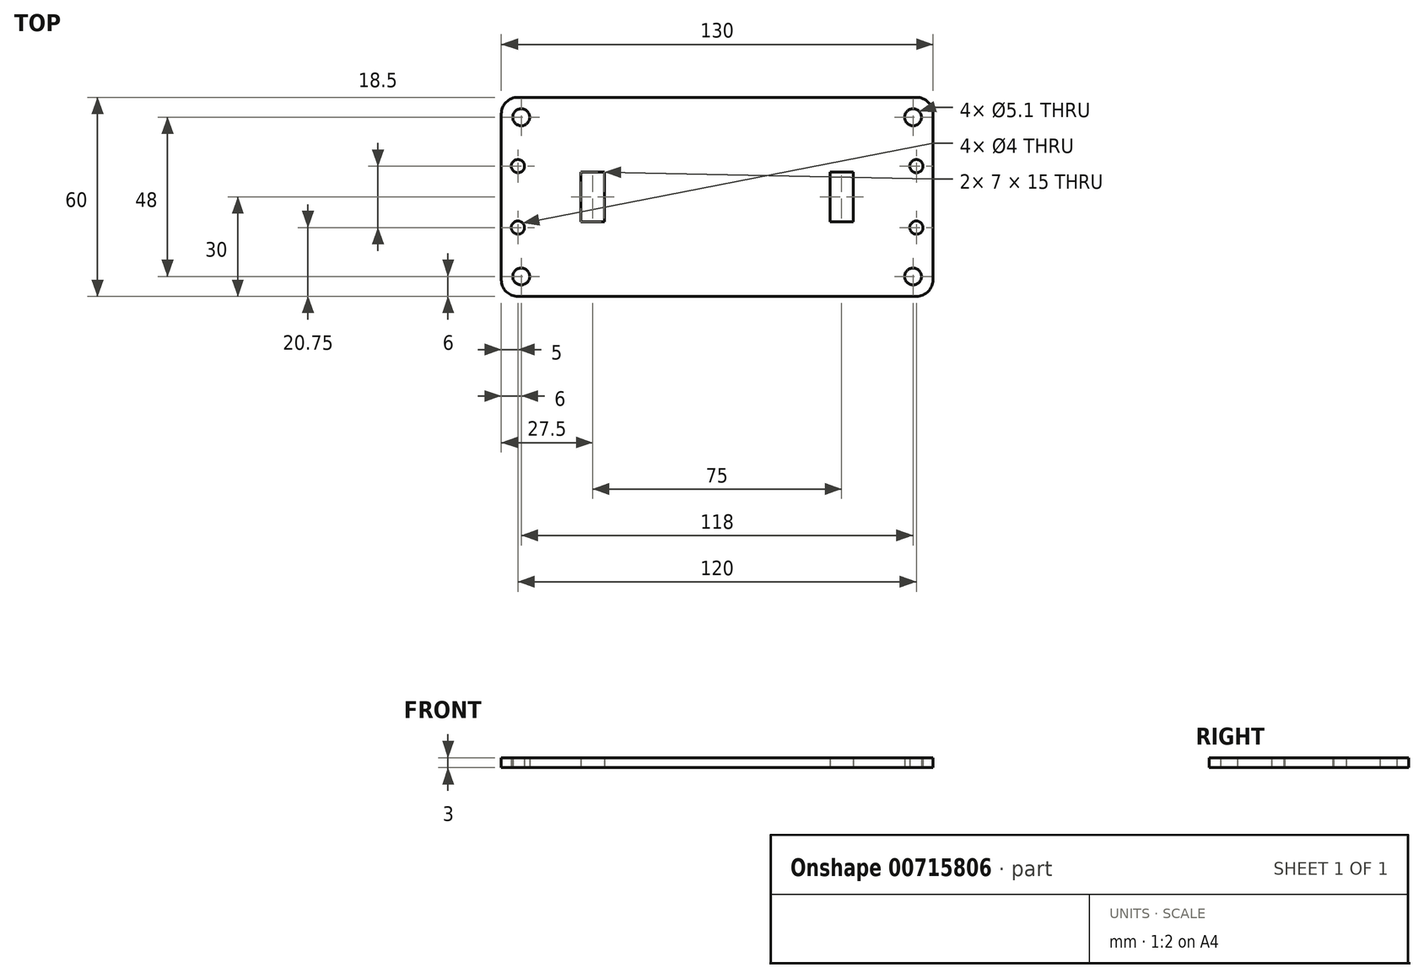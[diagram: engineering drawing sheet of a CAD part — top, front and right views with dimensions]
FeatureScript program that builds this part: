
annotation { "Feature Type Name" : "Feature", "Feature Type Description" : "" }
export const myFeature = defineFeature(function(context is Context, id is Id, definition is map)
    precondition{}
    {
        {
            var Q0;
            Q0=qCreatedBy(makeId("Top.planeOp"),FACE);
            var sketch = newSketch(context, id + "F0", { "sketchPlane" : qUnion([Q0])});
            skLineSegment(sketch, "E0.bottom", {"start": v(0, 0) * mm, "end": v(130, 0) * mm});
            skLineSegment(sketch, "E0.top", {"start": v(0, 60) * mm, "end": v(130, 60) * mm});
            skLineSegment(sketch, "E0.left", {"start": v(0, 0) * mm, "end": v(0, 60) * mm});
            skLineSegment(sketch, "E0.right", {"start": v(130, 0) * mm, "end": v(130, 60) * mm});
            skLineSegment(sketch, "E1", {"start": v(0, 30) * mm, "end": v(130, 30) * mm, "construction": true});
            skLineSegment(sketch, "E2", {"start": v(5, 39.25) * mm, "end": v(5, 30) * mm, "construction": true});
            skLineSegment(sketch, "E3", {"start": v(5, 39.25) * mm, "end": v(0, 39.25) * mm, "construction": true});
            skLineSegment(sketch, "E4", {"start": v(5, 20.75) * mm, "end": v(5, 30) * mm, "construction": true});
            skLineSegment(sketch, "E5", {"start": v(65, 60) * mm, "end": v(65, 0) * mm, "construction": true});
            skLineSegment(sketch, "E6", {"start": v(5, 39.25) * mm, "end": v(24, 39.25) * mm, "construction": true});
            skLineSegment(sketch, "E7", {"start": v(24, 39.25) * mm, "end": v(24, 36.25) * mm, "construction": true});
            skLineSegment(sketch, "E8.bottom", {"start": v(24, 37.5) * mm, "end": v(31, 37.5) * mm});
            skLineSegment(sketch, "E8.top", {"start": v(24, 22.5) * mm, "end": v(31, 22.5) * mm});
            skLineSegment(sketch, "E8.left", {"start": v(24, 37.5) * mm, "end": v(24, 22.5) * mm});
            skLineSegment(sketch, "E8.right", {"start": v(31, 37.5) * mm, "end": v(31, 22.5) * mm});
            skLineSegment(sketch, "E9.MirrorCS", {"start": v(106, 37.5) * mm, "end": v(99, 37.5) * mm});
            skLineSegment(sketch, "E10.MirrorCS", {"start": v(99, 37.5) * mm, "end": v(99, 22.5) * mm});
            skLineSegment(sketch, "E11.MirrorCS", {"start": v(106, 22.5) * mm, "end": v(99, 22.5) * mm});
            skLineSegment(sketch, "E12.MirrorCS", {"start": v(106, 37.5) * mm, "end": v(106, 22.5) * mm});
            skLineSegment(sketch, "E13", {"start": v(6, 54) * mm, "end": v(0, 54) * mm, "construction": true});
            skLineSegment(sketch, "E14", {"start": v(6, 54) * mm, "end": v(6, 60) * mm, "construction": true});
            skCircle(sketch, "E15", {"center": v(5, 39.25) * mm, "radius": 2 * mm});
            skCircle(sketch, "E16.MirrorC", {"center": v(5, 20.75) * mm, "radius": 2 * mm});
            skCircle(sketch, "E17.MirrorC", {"center": v(125, 39.25) * mm, "radius": 2 * mm});
            skCircle(sketch, "E18.MirrorC", {"center": v(125, 20.75) * mm, "radius": 2 * mm});
            skCircle(sketch, "E19", {"center": v(6, 54) * mm, "radius": 2.55 * mm});
            skCircle(sketch, "E20.MirrorC", {"center": v(6, 6) * mm, "radius": 2.55 * mm});
            skCircle(sketch, "E21.MirrorC", {"center": v(124, 54) * mm, "radius": 2.55 * mm});
            skCircle(sketch, "E22.MirrorC", {"center": v(124, 6) * mm, "radius": 2.55 * mm});
            skSolve(sketch);
        }
        {
            var Q0;
            Q0=makeQuery(id+"F0.imprint","IMPRINT",FACE,{"disambiguationData":[TD([[makeQuery(id+"F0.imprint","IMPRINT",EDGE,{"derivedFrom":sQuery(id+"F0.wireOp",EDGE,"E0.bottom")}),1.0]])]});
            extrude(context, id + "F1", {"entities" : qUnion([Q0]), "depth" : 3 * mm, "offsetDistance" : 25 * mm});
        }
        {
            var Q0;
            Q0=makeQuery(id+"F1.opExtrude","SWEPT_EDGE",EDGE,{"disambiguationData":[OSD([sQuery(id+"F0.wireOp",EDGE,"E0.bottom"),sQuery(id+"F0.wireOp",EDGE,"E0.right")])]});
            var Q1;
            Q1=makeQuery(id+"F1.opExtrude","SWEPT_EDGE",EDGE,{"disambiguationData":[OSD([sQuery(id+"F0.wireOp",EDGE,"E0.top"),sQuery(id+"F0.wireOp",EDGE,"E0.right")])]});
            var Q2;
            Q2=makeQuery(id+"F1.opExtrude","SWEPT_EDGE",EDGE,{"disambiguationData":[OSD([sQuery(id+"F0.wireOp",EDGE,"E0.bottom"),sQuery(id+"F0.wireOp",EDGE,"E0.left")])]});
            var Q3;
            Q3=makeQuery(id+"F1.opExtrude","SWEPT_EDGE",EDGE,{"disambiguationData":[OSD([sQuery(id+"F0.wireOp",EDGE,"E0.top"),sQuery(id+"F0.wireOp",EDGE,"E0.left")])]});
            fillet(context, id + "F2", {"entities" : qUnion([Q0, Q1, Q2, Q3]), "radius" : 5 * mm, "tangentPropagation" : true, "allowEdgeOverflow" : false});
        }
    });
